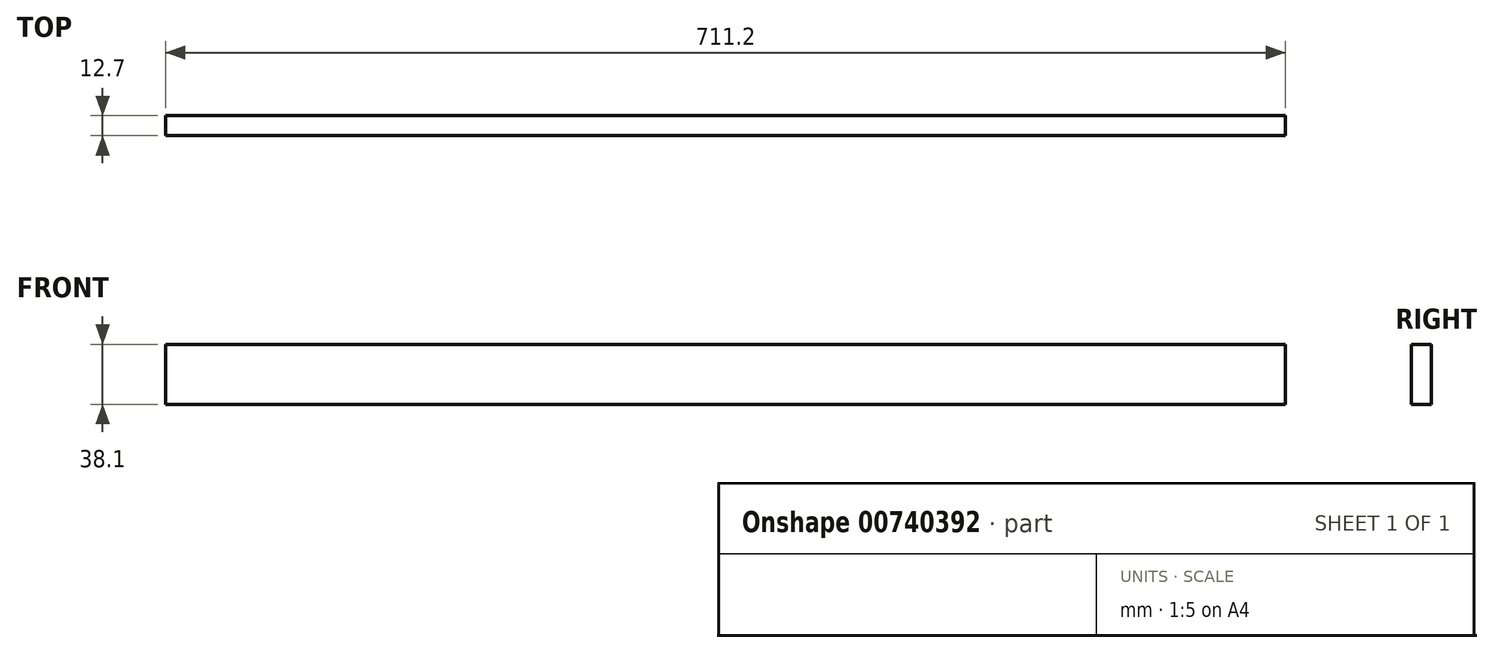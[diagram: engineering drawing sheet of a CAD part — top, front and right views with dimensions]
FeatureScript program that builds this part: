
annotation { "Feature Type Name" : "Feature", "Feature Type Description" : "" }
export const myFeature = defineFeature(function(context is Context, id is Id, definition is map)
    precondition{}
    {
        {
            var Q0;
            Q0=qCreatedBy(makeId("Front.planeOp"),FACE);
            var sketch = newSketch(context, id + "F0", { "sketchPlane" : qUnion([Q0])});
            skLineSegment(sketch, "E0.bottom", {"start": v(355.6, 19.05) * mm, "end": v(-355.6, 19.05) * mm});
            skLineSegment(sketch, "E0.top", {"start": v(355.6, -19.05) * mm, "end": v(-355.6, -19.05) * mm});
            skLineSegment(sketch, "E0.left", {"start": v(355.6, 19.05) * mm, "end": v(355.6, -19.05) * mm});
            skLineSegment(sketch, "E0.right", {"start": v(-355.6, 19.05) * mm, "end": v(-355.6, -19.05) * mm});
            skPoint(sketch, "E0.middle", {"position": v(0, 0) * mm});
            skSolve(sketch);
        }
        {
            var Q0;
            Q0=makeQuery(id+"F0.imprint","IMPRINT",FACE,{"disambiguationData":[TD([[makeQuery(id+"F0.imprint","IMPRINT",EDGE,{"derivedFrom":sQuery(id+"F0.wireOp",EDGE,"E0.bottom")}),1.0]])]});
            extrude(context, id + "F1", {"entities" : qUnion([Q0]), "depth" : 12.7 * mm, "offsetDistance" : 25.4 * mm});
        }
    });
